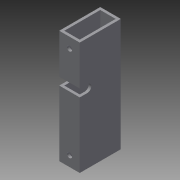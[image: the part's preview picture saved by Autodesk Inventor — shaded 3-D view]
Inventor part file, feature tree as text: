
AUTODESK INVENTOR PART (.ipt)
format: ipt  version: 2015 (Build 190159000, 159)  size: 110,080 bytes
history: native  units: in
note: dims shown in document units (in); Inventor stores cm internally (conversion verified against a paired STEP export)
features: sketch x3, extrude x2, projected_geometry x2, hole x1
ambient origin geometry x8: Origin, YZ Plane, XZ Plane, XY Plane, X Axis, Y Axis, Z Axis, Center Point
bodies: Solid1 (feature_tree)
feature tree (8):
  extrude  "Extrusion1"  Depth=2.0in
  hole  "Hole1"  [1 undecoded]
  extrude  "Extrusion2"  Depth=0.125in
  sketch  "Sketch1"  dims[d0=1.0in d1=2.0in]
  sketch  "Sketch2"  dims[d2=0.75in d3=1.75in]
  projected_geometry  "Projected Loop1"
  sketch  "Sketch3"  dims[d4=0.125in d5=0.125in d6=5.5in d7=0.0in d8=0.5in d9=0.5in d10=0.5in d11=0.5in d12=0.25in d13=0.75in d14=0.375in d15=0.25in d16=0.5635in d17=1.0in d18=0.8108in d19=2.75in d20=0.375in d21=0.375in d22=6.125in d23=0.0in]
  projected_geometry  "Projected Loop2"
note: 1 required parameter value undecoded (feature->parameter linkage not recoverable at this tier; creation-order binding heuristic only, values carry confidence <= 0.55)
